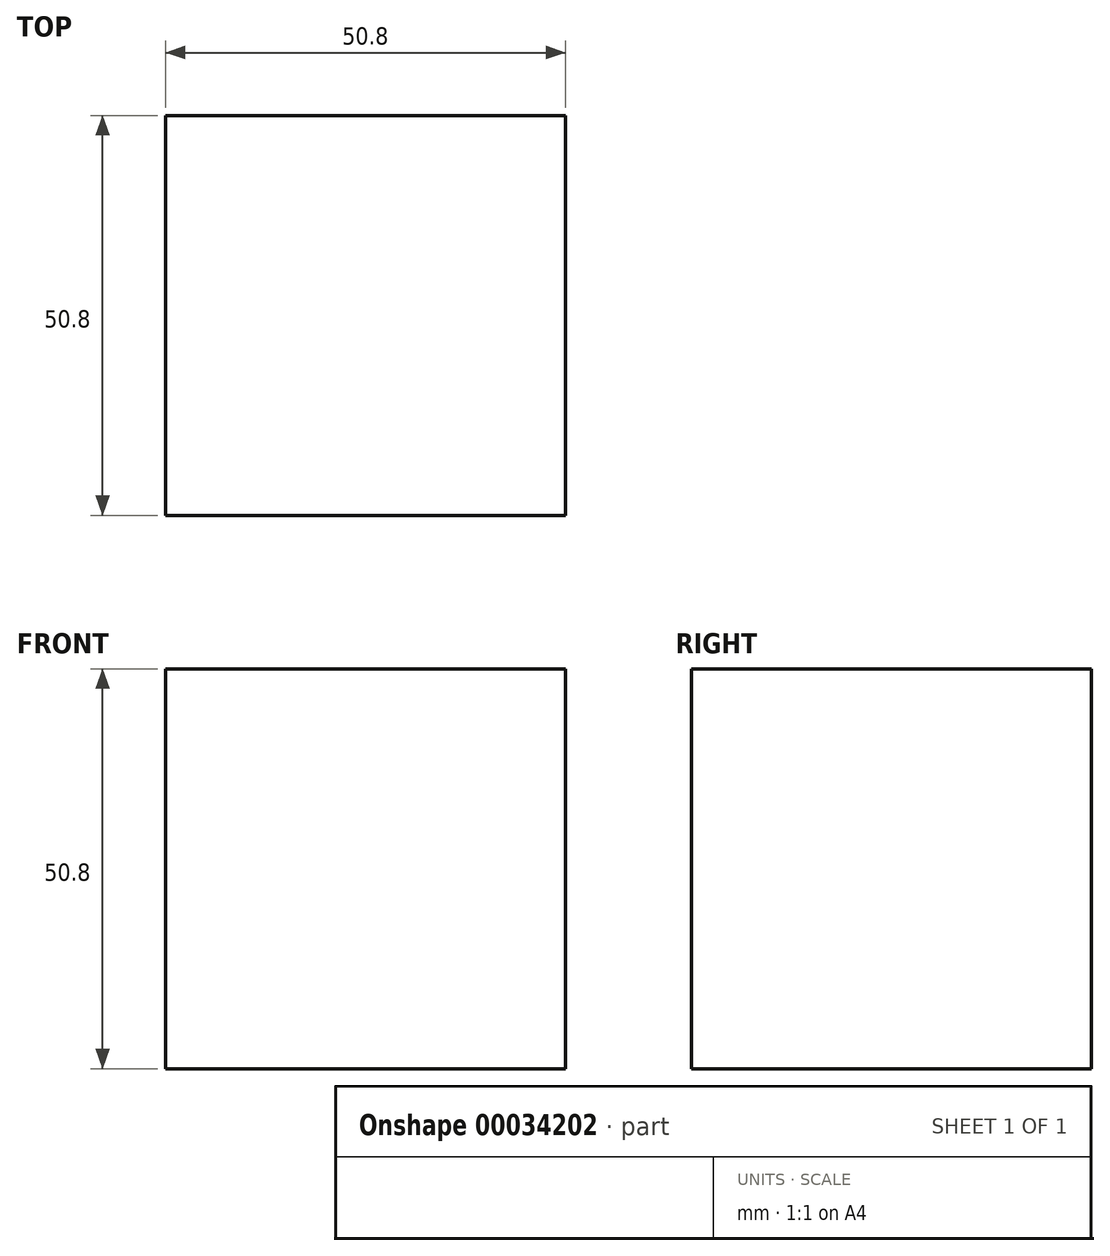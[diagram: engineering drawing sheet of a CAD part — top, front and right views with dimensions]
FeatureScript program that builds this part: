
annotation { "Feature Type Name" : "Feature", "Feature Type Description" : "" }
export const myFeature = defineFeature(function(context is Context, id is Id, definition is map)
    precondition{}
    {
        {
            var Q0;
            Q0=qCreatedBy(makeId("Top.planeOp"),FACE);
            var sketch = newSketch(context, id + "F0", { "sketchPlane" : qUnion([Q0])});
            skLineSegment(sketch, "E0.bottom", {"start": v(0, 0) * mm, "end": v(50.8, 0) * mm});
            skLineSegment(sketch, "E0.top", {"start": v(0, 50.8) * mm, "end": v(50.8, 50.8) * mm});
            skLineSegment(sketch, "E0.left", {"start": v(0, 0) * mm, "end": v(0, 50.8) * mm});
            skLineSegment(sketch, "E0.right", {"start": v(50.8, 0) * mm, "end": v(50.8, 50.8) * mm});
            skSolve(sketch);
        }
        {
            var Q0;
            Q0=makeQuery(id+"F0.imprint","IMPRINT",FACE,{"disambiguationData":[TD([[makeQuery(id+"F0.imprint","IMPRINT",EDGE,{"derivedFrom":sQuery(id+"F0.wireOp",EDGE,"E0.bottom")}),1.0]])]});
            extrude(context, id + "F1", {"entities" : qUnion([Q0]), "depth" : 50.8 * mm});
        }
    });
